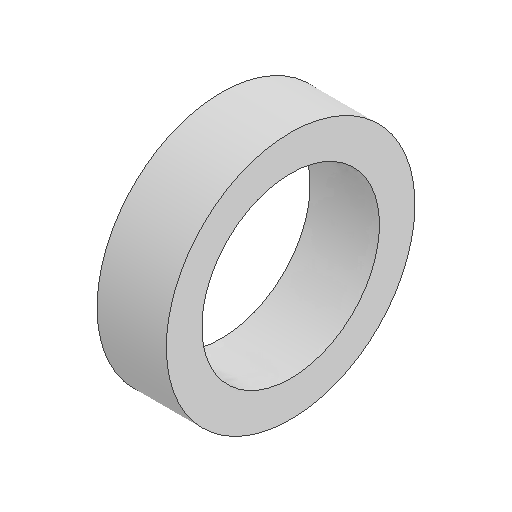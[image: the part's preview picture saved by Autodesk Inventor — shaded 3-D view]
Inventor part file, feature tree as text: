
AUTODESK INVENTOR PART (.ipt)
format: ipt  version: 2025.1 (Build 291241000, 241)  size: 97,280 bytes
history: native  units: mm
features: other x1, extrude x1, sketch x1
ambient origin geometry x8: Origin, YZ Plane, XZ Plane, XY Plane, X Axis, Y Axis, Z Axis, Center Point
bodies: Body1 (feature_tree)
feature tree (3):
  other  "Bryła1"
  extrude  "Wyciągnięcie proste1"  Depth=5.0mm
  sketch  "Szkic1"
